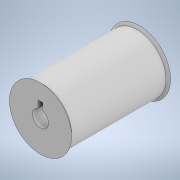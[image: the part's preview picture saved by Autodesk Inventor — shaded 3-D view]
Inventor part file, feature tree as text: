
AUTODESK INVENTOR PART (.ipt)
format: ipt  version: 2021 (Build 250183000, 183)  size: 127,488 bytes
history: native  units: mm
features: sketch x3, extrude x2, other x1, revolve x1
ambient origin geometry x8: Origin, YZ Plane, XZ Plane, XY Plane, X Axis, Y Axis, Z Axis, Center Point
bodies: Body1 (feature_tree)
feature tree (7):
  other  "Твердое тело1"
  extrude  "Выдавливание1"  Depth=25.0mm
  extrude  "Выдавливание2"  Depth=7.0mm
  revolve  "Вращение1"
  sketch  "Эскиз1"
  sketch  "Эскиз2"
  sketch  "Эскиз3"
